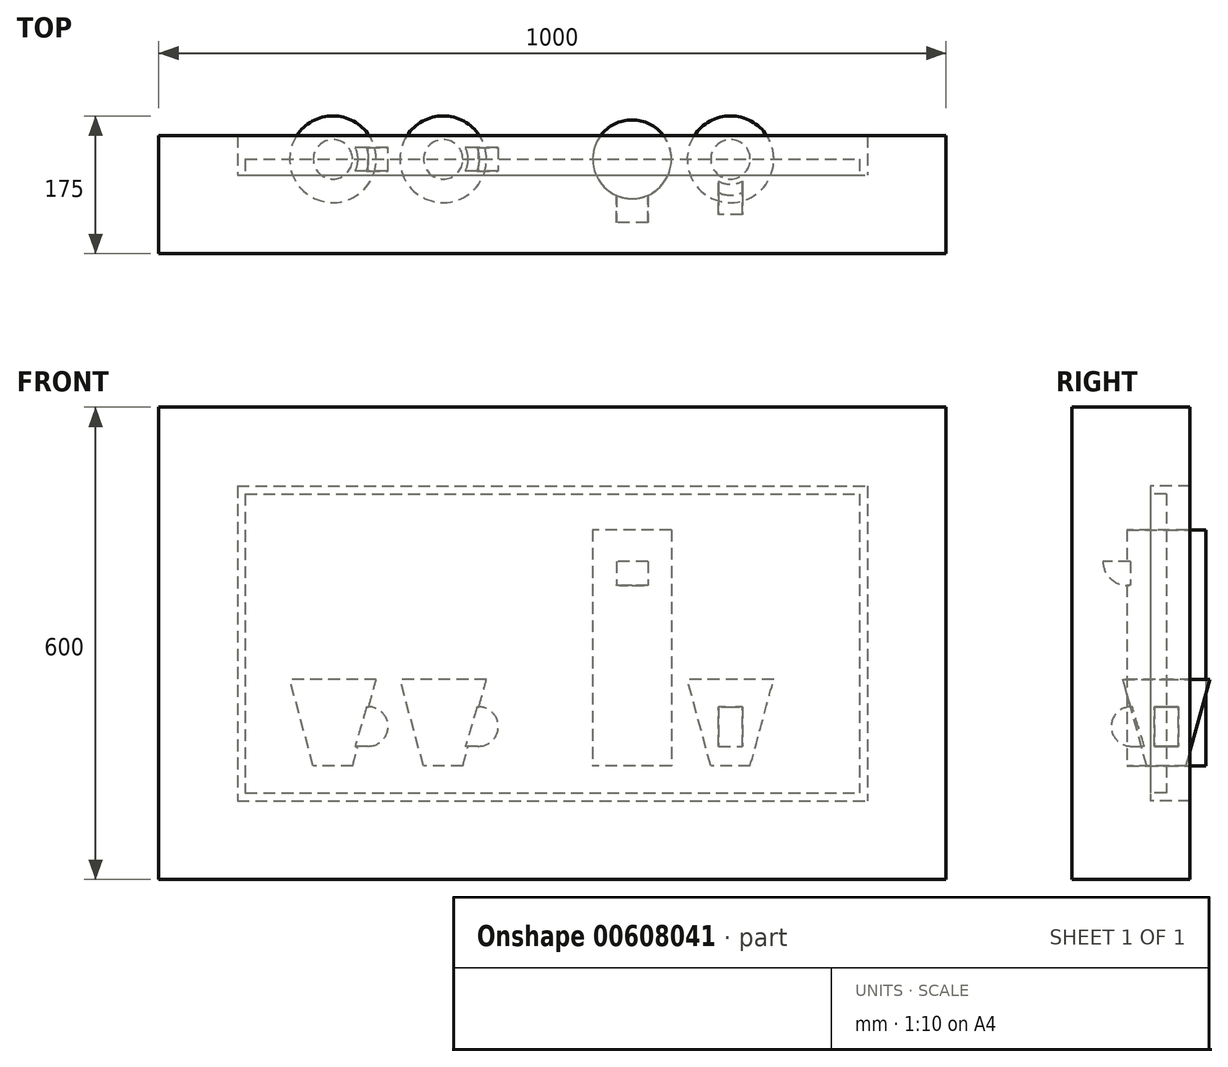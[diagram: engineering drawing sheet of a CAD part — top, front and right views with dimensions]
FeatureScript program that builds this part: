
annotation { "Feature Type Name" : "Feature", "Feature Type Description" : "" }
export const myFeature = defineFeature(function(context is Context, id is Id, definition is map)
    precondition{}
    {
        {
            var Q0;
            Q0=qCreatedBy(makeId("Top.planeOp"),FACE);
            cPlane(context, id + "F0", {"entities" : qUnion([Q0]), "cplaneType" : CPlaneType.OFFSET, "offset" : 110 * mm, "width" : 150 * mm, "height" : 150 * mm});
        }
        {
            var Q0;
            Q0=qCreatedBy(makeId("Top.planeOp"),FACE);
            var sketch = newSketch(context, id + "F1", { "sketchPlane" : qUnion([Q0])});
            skCircle(sketch, "E0", {"center": v(80, 0) * mm, "radius": 50 * mm});
            skSolve(sketch);
        }
        {
            var Q0;
            Q0=qSketchRegion(id+"F1",true);
            var Q1;
            Q1=qSketchRegion(id+"F3",true);
            extrude(context, id + "F2", {"entities" : qUnion([Q0, Q1]), "depth" : 300 * mm, "offsetDistance" : 25 * mm});
        }
        {
            var Q0;
            Q0=qCreatedBy(makeId("Top.planeOp"),FACE);
            var sketch = newSketch(context, id + "F3", { "sketchPlane" : qUnion([Q0])});
            skCircle(sketch, "E1", {"center": v(205, 0) * mm, "radius": 25 * mm});
            skSolve(sketch);
        }
        {
            var Q0;
            Q0=qCreatedBy(id+"F0.planeOp",FACE);
            var sketch = newSketch(context, id + "F4", { "sketchPlane" : qUnion([Q0])});
            skCircle(sketch, "E2", {"center": v(205, 0) * mm, "radius": 55 * mm});
            skSolve(sketch);
        }
        {
            var Q0;
            Q0=qSketchRegion(id+"F3",true);
            var Q1;
            Q1=qSketchRegion(id+"F4",true);
            loft(context, id + "F5", {"sheetProfilesArray" : [{ "sheetProfileEntities" : qUnion([Q0]) }, { "sheetProfileEntities" : qUnion([Q1]) }]});
        }
        {
            var Q0;
            Q0=qCreatedBy(makeId("Top.planeOp"),FACE);
            var sketch = newSketch(context, id + "F6", { "sketchPlane" : qUnion([Q0])});
            skCircle(sketch, "E3", {"center": v(-160, 0) * mm, "radius": 25 * mm});
            skSolve(sketch);
        }
        {
            var Q0;
            Q0=qCreatedBy(id+"F0.planeOp",FACE);
            var sketch = newSketch(context, id + "F7", { "sketchPlane" : qUnion([Q0])});
            skCircle(sketch, "E4", {"center": v(-160, 0) * mm, "radius": 55 * mm});
            skSolve(sketch);
        }
        {
            var Q0;
            Q0=qSketchRegion(id+"F6",true);
            var Q1;
            Q1=qSketchRegion(id+"F7",true);
            loft(context, id + "F8", {"sheetProfilesArray" : [{ "sheetProfileEntities" : qUnion([Q0]) }, { "sheetProfileEntities" : qUnion([Q1]) }]});
        }
        {
            var Q0;
            Q0=qCreatedBy(makeId("Top.planeOp"),FACE);
            var sketch = newSketch(context, id + "F9", { "sketchPlane" : qUnion([Q0])});
            skCircle(sketch, "E5", {"center": v(-300, 0) * mm, "radius": 25 * mm});
            skSolve(sketch);
        }
        {
            var Q0;
            Q0=qCreatedBy(id+"F0.planeOp",FACE);
            var sketch = newSketch(context, id + "F10", { "sketchPlane" : qUnion([Q0])});
            skCircle(sketch, "E6", {"center": v(-300, 0) * mm, "radius": 55 * mm});
            skSolve(sketch);
        }
        {
            var Q0;
            Q0=qSketchRegion(id+"F9",true);
            var Q1;
            Q1=qSketchRegion(id+"F10",true);
            loft(context, id + "F11", {"sheetProfilesArray" : [{ "sheetProfileEntities" : qUnion([Q0]) }, { "sheetProfileEntities" : qUnion([Q1]) }]});
        }
        {
            var Q0;
            Q0=qCreatedBy(makeId("Right.planeOp"),FACE);
            cPlane(context, id + "F12", {"entities" : qUnion([Q0]), "cplaneType" : CPlaneType.OFFSET, "offset" : 80 * mm, "width" : 150 * mm, "height" : 150 * mm});
        }
        {
            var Q0;
            Q0=qCreatedBy(id+"F12.planeOp",FACE);
            var sketch = newSketch(context, id + "F13", { "sketchPlane" : qUnion([Q0])});
            skArc(sketch, "E7", {"start": v(-80.58, 259.93) * mm, "mid": v(-50, 229.42) * mm, "end": v(-19.42, 259.93) * mm});
            skLineSegment(sketch, "E8", {"start": v(-19.42, 259.93) * mm, "end": v(-80.58, 259.93) * mm});
            skSolve(sketch);
        }
        {
            var Q0;
            Q0=qSketchRegion(id+"F13",true);
            extrude(context, id + "F14", {"entities" : qUnion([Q0]), "operationType" : NewBodyOperationType.ADD, "endBound" : BoundingType.SYMMETRIC, "depth" : 40 * mm, "offsetDistance" : 25 * mm});
        }
        {
            var Q0;
            Q0=qCreatedBy(makeId("Right.planeOp"),FACE);
            cPlane(context, id + "F15", {"entities" : qUnion([Q0]), "cplaneType" : CPlaneType.OFFSET, "offset" : 205 * mm, "width" : 150 * mm, "height" : 150 * mm});
        }
        {
            var Q0;
            Q0=qCreatedBy(id+"F15.planeOp",FACE);
            var sketch = newSketch(context, id + "F16", { "sketchPlane" : qUnion([Q0])});
            skArc(sketch, "E9", {"start": v(-44.02, 74.98) * mm, "mid": v(-69.99, 50.74) * mm, "end": v(-45.51, 25) * mm});
            skLineSegment(sketch, "E10", {"start": v(-45.51, 25) * mm, "end": v(-13.64, 24.35) * mm});
            skLineSegment(sketch, "E11", {"start": v(-13.64, 24.35) * mm, "end": v(-13.64, 73.8) * mm});
            skLineSegment(sketch, "E12", {"start": v(-13.64, 73.8) * mm, "end": v(-44.02, 74.98) * mm});
            skSolve(sketch);
        }
        {
            var Q0;
            Q0=qSketchRegion(id+"F16",true);
            extrude(context, id + "F17", {"entities" : qUnion([Q0]), "operationType" : NewBodyOperationType.ADD, "endBound" : BoundingType.SYMMETRIC, "depth" : 30 * mm, "offsetDistance" : 25 * mm});
        }
        {
            var Q0;
            Q0=qCreatedBy(makeId("Front.planeOp"),FACE);
            var sketch = newSketch(context, id + "F18", { "sketchPlane" : qUnion([Q0])});
            skArc(sketch, "E13", {"start": v(-115.89, 25.02) * mm, "mid": v(-90, 49.5) * mm, "end": v(-114.88, 75) * mm});
            skLineSegment(sketch, "E14", {"start": v(-115.89, 25.02) * mm, "end": v(-153.4, 25.02) * mm});
            skLineSegment(sketch, "E15", {"start": v(-153.4, 25.02) * mm, "end": v(-153.4, 75.18) * mm});
            skLineSegment(sketch, "E16", {"start": v(-153.4, 75.18) * mm, "end": v(-114.88, 75) * mm});
            skSolve(sketch);
        }
        {
            var Q0;
            Q0=qSketchRegion(id+"F18",true);
            extrude(context, id + "F19", {"entities" : qUnion([Q0]), "operationType" : NewBodyOperationType.ADD, "endBound" : BoundingType.SYMMETRIC, "oppositeDirection" : true, "depth" : 30 * mm, "offsetDistance" : 25 * mm});
        }
        {
            var Q0;
            Q0=qCreatedBy(makeId("Front.planeOp"),FACE);
            var sketch = newSketch(context, id + "F20", { "sketchPlane" : qUnion([Q0])});
            skArc(sketch, "E17", {"start": v(-255.26, 25) * mm, "mid": v(-230, 50.18) * mm, "end": v(-255.62, 75) * mm});
            skLineSegment(sketch, "E18", {"start": v(-254.74, 25) * mm, "end": v(-297.4, 25) * mm});
            skLineSegment(sketch, "E19", {"start": v(-297.4, 25) * mm, "end": v(-297.4, 73.96) * mm});
            skLineSegment(sketch, "E20", {"start": v(-297.4, 73.96) * mm, "end": v(-255.62, 75) * mm});
            skSolve(sketch);
        }
        {
            var Q0;
            Q0 = qSketchRegion(id + "F20", true);
            extrude(context, id + "F21", {"entities" : qUnion([Q0]), "operationType" : NewBodyOperationType.ADD, "endBound" : BoundingType.SYMMETRIC, "depth" : 30 * mm, "offsetDistance" : 25 * mm});
        }
        {
            var Q0;
            Q0=qCreatedBy(makeId("Front.planeOp"),FACE);
            cPlane(context, id + "F22", {"entities" : qUnion([Q0]), "cplaneType" : CPlaneType.OFFSET, "offset" : 20 * mm, "width" : 150 * mm, "height" : 150 * mm});
        }
        {
            var Q0;
            Q0=qCreatedBy(id+"F22.planeOp",FACE);
            var sketch = newSketch(context, id + "F23", { "sketchPlane" : qUnion([Q0])});
            skLineSegment(sketch, "E21.bottom", {"start": v(-421.33, 355.64) * mm, "end": v(378.67, 355.64) * mm});
            skLineSegment(sketch, "E21.top", {"start": v(-421.33, -44.36) * mm, "end": v(378.67, -44.36) * mm});
            skLineSegment(sketch, "E21.left", {"start": v(-421.33, 355.64) * mm, "end": v(-421.33, -44.36) * mm});
            skLineSegment(sketch, "E21.right", {"start": v(378.67, 355.64) * mm, "end": v(378.67, -44.36) * mm});
            skSolve(sketch);
        }
        {
            var Q0;
            Q0=qCreatedBy(makeId("Front.planeOp"),FACE);
            cPlane(context, id + "F24", {"entities" : qUnion([Q0]), "cplaneType" : CPlaneType.OFFSET, "offset" : 30 * mm, "oppositeDirection" : true, "width" : 150 * mm, "height" : 150 * mm});
        }
        {
            var Q0;
            Q0=qSketchRegion(id+"F23",true);
            extrude(context, id + "F25", {"entities" : qUnion([Q0]), "oppositeDirection" : true, "depth" : 60 * mm, "offsetDistance" : 25 * mm});
        }
        {
            var Q0;
            Q0=qCreatedBy(id+"F22.planeOp",FACE);
            var sketch = newSketch(context, id + "F26", { "sketchPlane" : qUnion([Q0])});
            skLineSegment(sketch, "E22.bottom", {"start": v(-411.33, 345.64) * mm, "end": v(368.67, 345.64) * mm});
            skLineSegment(sketch, "E22.top", {"start": v(-411.33, -34.36) * mm, "end": v(368.67, -34.36) * mm});
            skLineSegment(sketch, "E22.left", {"start": v(-411.33, 345.64) * mm, "end": v(-411.33, -34.36) * mm});
            skLineSegment(sketch, "E22.right", {"start": v(368.67, 345.64) * mm, "end": v(368.67, -34.36) * mm});
            skSolve(sketch);
        }
        {
            var Q0;
            Q0 = qSketchRegion(id + "F26", true);
            extrude(context, id + "F27", {"entities" : qUnion([Q0]), "oppositeDirection" : true, "depth" : 20 * mm, "offsetDistance" : 25 * mm});
        }
        {
            var Q0;
            Q0=qCreatedBy(id+"F24.planeOp",FACE);
            var sketch = newSketch(context, id + "F28", { "sketchPlane" : qUnion([Q0])});
            skLineSegment(sketch, "E23.bottom", {"start": v(-521.33, 455.64) * mm, "end": v(478.67, 455.64) * mm});
            skLineSegment(sketch, "E23.top", {"start": v(-521.33, -144.36) * mm, "end": v(478.67, -144.36) * mm});
            skLineSegment(sketch, "E23.left", {"start": v(-521.33, 455.64) * mm, "end": v(-521.33, -144.36) * mm});
            skLineSegment(sketch, "E23.right", {"start": v(478.67, 455.64) * mm, "end": v(478.67, -144.36) * mm});
            skSolve(sketch);
        }
        {
            var Q0;
            Q0 = qSketchRegion(id + "F28", true);
            extrude(context, id + "F29", {"entities" : qUnion([Q0]), "depth" : 150 * mm, "offsetDistance" : 25 * mm});
        }
        {
            var Q0;
            Q0=makeQuery(id+"F27.opExtrude","SWEPT_BODY",BODY,{"disambiguationData":[OSD([sQuery(id+"F26.wireOp",EDGE,"E22.bottom"),sQuery(id+"F26.wireOp",EDGE,"E22.top"),sQuery(id+"F26.wireOp",EDGE,"E22.left"),sQuery(id+"F26.wireOp",EDGE,"E22.right")])]});
            var Q1;
            Q1=makeQuery(id+"F25.opExtrude","SWEPT_BODY",BODY,{"disambiguationData":[OSD([sQuery(id+"F23.wireOp",EDGE,"E21.bottom"),sQuery(id+"F23.wireOp",EDGE,"E21.top"),sQuery(id+"F23.wireOp",EDGE,"E21.left"),sQuery(id+"F23.wireOp",EDGE,"E21.right")])]});
            booleanBodies(context, id + "F30", {"operationType" : BooleanOperationType.SUBTRACTION, "tools" : qUnion([Q0]), "targets" : qUnion([Q1])});
        }
        {
            var Q0;
            Q0=makeQuery(id+"F25.opExtrude","SWEPT_BODY",BODY,{"disambiguationData":[OSD([sQuery(id+"F23.wireOp",EDGE,"E21.bottom"),sQuery(id+"F23.wireOp",EDGE,"E21.top"),sQuery(id+"F23.wireOp",EDGE,"E21.left"),sQuery(id+"F23.wireOp",EDGE,"E21.right")])]});
            var Q1;
            Q1=makeQuery(id+"F29.opExtrude","SWEPT_BODY",BODY,{"disambiguationData":[OSD([sQuery(id+"F28.wireOp",EDGE,"E23.bottom"),sQuery(id+"F28.wireOp",EDGE,"E23.top"),sQuery(id+"F28.wireOp",EDGE,"E23.left"),sQuery(id+"F28.wireOp",EDGE,"E23.right")])]});
            booleanBodies(context, id + "F31", {"operationType" : BooleanOperationType.SUBTRACTION, "tools" : qUnion([Q0]), "targets" : qUnion([Q1])});
        }
    });
